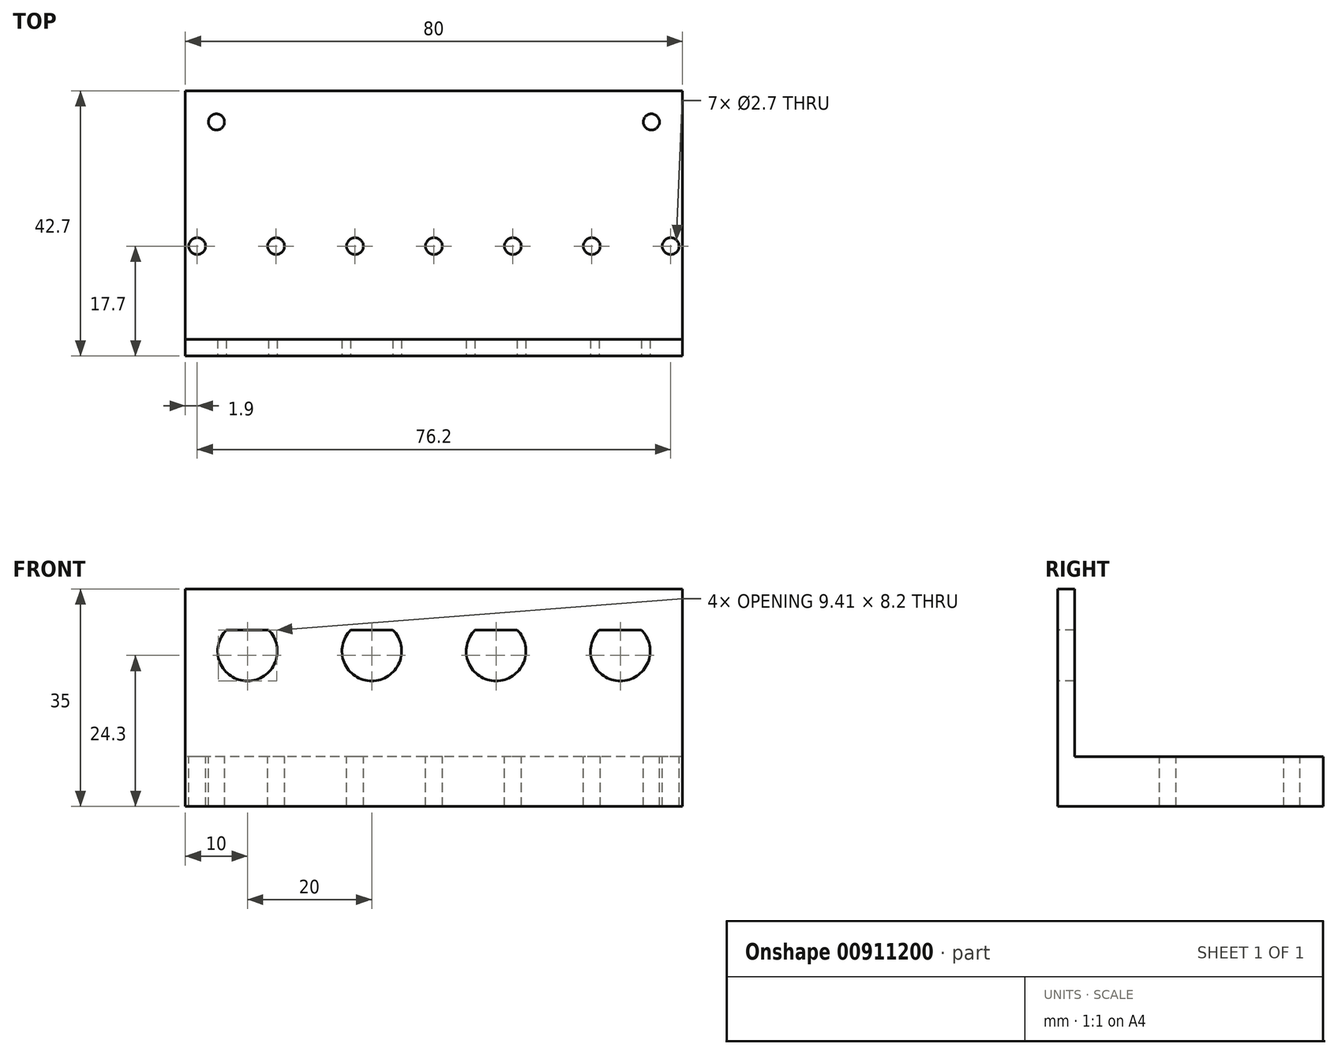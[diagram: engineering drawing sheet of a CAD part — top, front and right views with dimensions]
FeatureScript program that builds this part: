
annotation { "Feature Type Name" : "Feature", "Feature Type Description" : "" }
export const myFeature = defineFeature(function(context is Context, id is Id, definition is map)
    precondition{}
    {
        {
            var Q0;
            Q0=qCreatedBy(makeId("Right.planeOp"),FACE);
            var sketch = newSketch(context, id + "F0", { "sketchPlane" : qUnion([Q0])});
            skLineSegment(sketch, "E0", {"start": v(0, 0) * mm, "end": v(42.7, 0) * mm});
            skLineSegment(sketch, "E1", {"start": v(42.7, 0) * mm, "end": v(42.7, 8) * mm});
            skLineSegment(sketch, "E2", {"start": v(42.7, 8) * mm, "end": v(2.7, 8) * mm});
            skLineSegment(sketch, "E3", {"start": v(2.7, 8) * mm, "end": v(2.7, 35) * mm});
            skLineSegment(sketch, "E4", {"start": v(2.7, 35) * mm, "end": v(0, 35) * mm});
            skLineSegment(sketch, "E5", {"start": v(0, 35) * mm, "end": v(0, 0) * mm});
            skSolve(sketch);
        }
        {
            var Q0;
            Q0 = qSketchRegion(id + "F0", true);
            extrude(context, id + "F1", {"entities" : qUnion([Q0]), "depth" : 80 * mm, "offsetDistance" : 25 * mm});
        }
        {
            var Q0;
            Q0=makeQuery(id+"F1.opExtrude","SWEPT_FACE",FACE,{"disambiguationData":[OSD([sQuery(id+"F0.wireOp",EDGE,"E5")])]});
            var sketch = newSketch(context, id + "F2", { "sketchPlane" : qUnion([Q0])});
            skLineSegment(sketch, "E6", {"start": v(-8.63, 25) * mm, "end": v(91.97, 25) * mm, "construction": true});
            skArc(sketch, "E7", {"start": v(6.61, 28.4) * mm, "mid": v(10, 20.2) * mm, "end": v(13.39, 28.4) * mm});
            skArc(sketch, "E8", {"start": v(26.61, 28.4) * mm, "mid": v(30, 20.2) * mm, "end": v(33.39, 28.4) * mm});
            skArc(sketch, "E9", {"start": v(46.61, 28.4) * mm, "mid": v(50, 20.2) * mm, "end": v(53.39, 28.4) * mm});
            skArc(sketch, "E10", {"start": v(66.61, 28.4) * mm, "mid": v(70, 20.2) * mm, "end": v(73.39, 28.4) * mm});
            skLineSegment(sketch, "E11", {"start": v(40, 42.16) * mm, "end": v(40, -7.88) * mm, "construction": true});
            skPoint(sketch, "E11.startSnap0", {"position": v(40, 35) * mm});
            skPoint(sketch, "E11.endSnap0", {"position": v(40, 0) * mm});
            skLineSegment(sketch, "E12", {"start": v(6.61, 28.4) * mm, "end": v(13.39, 28.4) * mm});
            skLineSegment(sketch, "E13.trimOffspring", {"start": v(66.61, 28.4) * mm, "end": v(73.39, 28.4) * mm});
            skLineSegment(sketch, "E14.trimOffspring", {"start": v(46.61, 28.4) * mm, "end": v(53.39, 28.4) * mm});
            skLineSegment(sketch, "E15.trimOffspring", {"start": v(26.61, 28.4) * mm, "end": v(33.39, 28.4) * mm});
            skPoint(sketch, "E16.orphan", {"position": v(2.69, 28.4) * mm});
            skSolve(sketch);
        }
        {
            var Q0;
            Q0 = qSketchRegion(id + "F2", true);
            extrude(context, id + "F3", {"entities" : qUnion([Q0]), "operationType" : NewBodyOperationType.REMOVE, "endBound" : BoundingType.THROUGH_ALL, "oppositeDirection" : true, "depth" : 25 * mm, "offsetDistance" : 25 * mm});
        }
        {
            var Q0;
            Q0=makeQuery(id+"F1.opExtrude","SWEPT_FACE",FACE,{"disambiguationData":[OSD([sQuery(id+"F0.wireOp",EDGE,"E2")])]});
            var sketch = newSketch(context, id + "F4", { "sketchPlane" : qUnion([Q0])});
            skCircle(sketch, "E17", {"center": v(5, 37.7) * mm, "radius": 1.3 * mm});
            skCircle(sketch, "E18", {"center": v(75, 37.7) * mm, "radius": 1.3 * mm});
            skLineSegment(sketch, "E19", {"start": v(-2.39, 37.7) * mm, "end": v(82.33, 37.7) * mm, "construction": true});
            skLineSegment(sketch, "E20", {"start": v(40, 49.93) * mm, "end": v(40, -11.82) * mm, "construction": true});
            skPoint(sketch, "E20.startSnap0", {"position": v(40, 42.7) * mm});
            skLineSegment(sketch, "E21", {"start": v(-5.29, 17.7) * mm, "end": v(85.29, 17.7) * mm, "construction": true});
            skCircle(sketch, "E22", {"center": v(14.6, 17.7) * mm, "radius": 1.35 * mm});
            skCircle(sketch, "E23", {"center": v(27.3, 17.7) * mm, "radius": 1.35 * mm});
            skCircle(sketch, "E24", {"center": v(1.9, 17.7) * mm, "radius": 1.35 * mm});
            skCircle(sketch, "E25", {"center": v(40, 17.7) * mm, "radius": 1.35 * mm});
            skCircle(sketch, "E26.MirrorC", {"center": v(52.7, 17.7) * mm, "radius": 1.35 * mm});
            skCircle(sketch, "E27.MirrorC", {"center": v(65.4, 17.7) * mm, "radius": 1.35 * mm});
            skCircle(sketch, "E28.MirrorC", {"center": v(78.1, 17.7) * mm, "radius": 1.35 * mm});
            skSolve(sketch);
        }
        {
            var Q0;
            Q0 = qSketchRegion(id + "F4", true);
            extrude(context, id + "F5", {"entities" : qUnion([Q0]), "operationType" : NewBodyOperationType.REMOVE, "endBound" : BoundingType.THROUGH_ALL, "oppositeDirection" : true, "depth" : 25 * mm, "offsetDistance" : 25 * mm});
        }
    });
